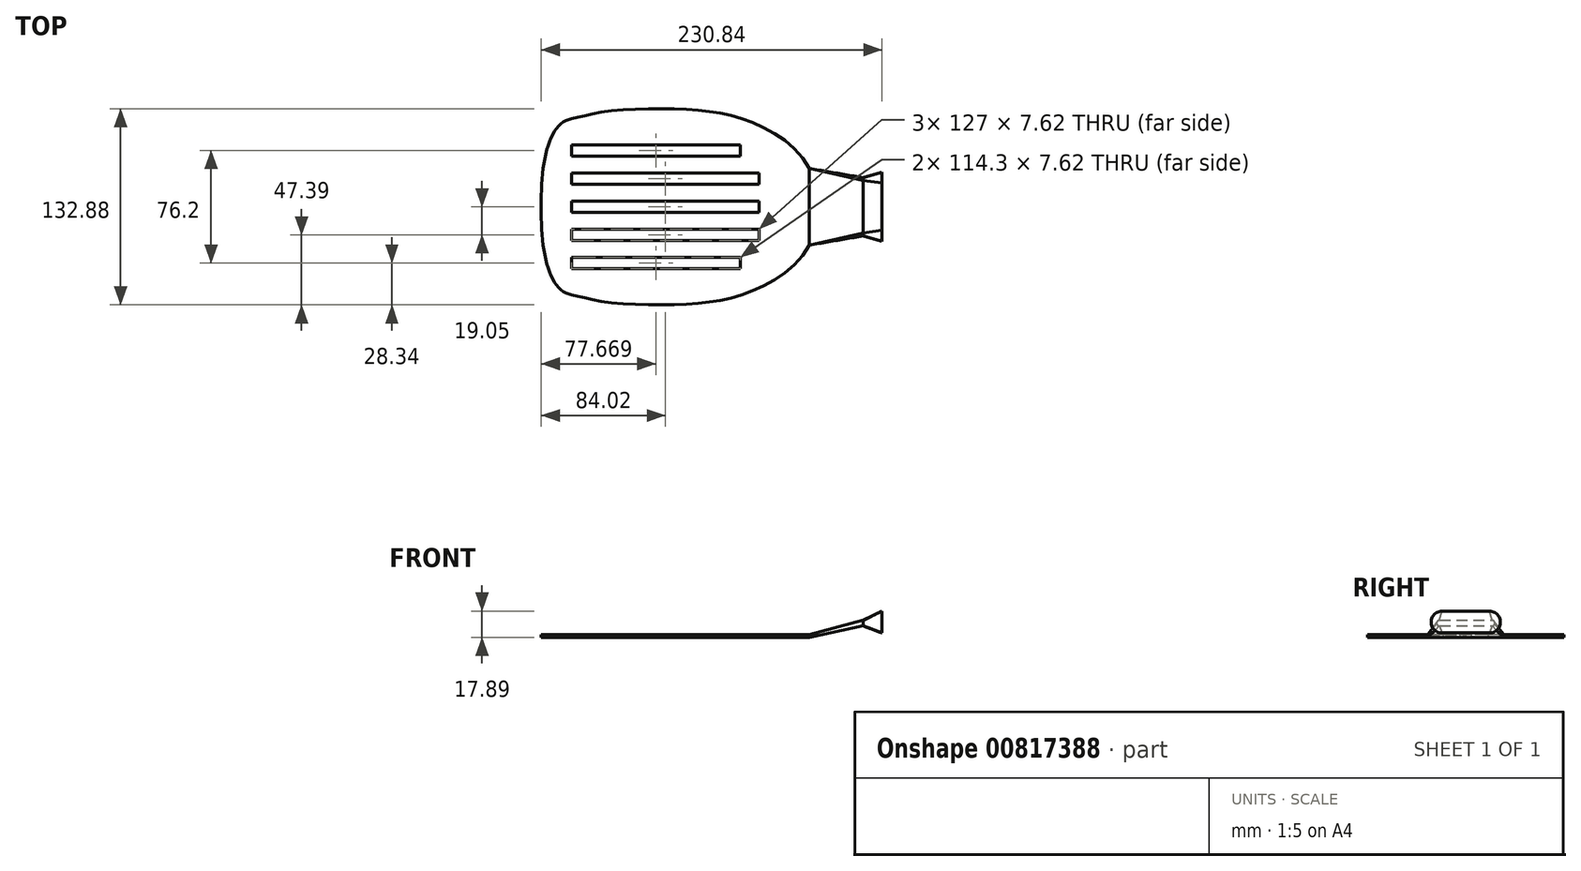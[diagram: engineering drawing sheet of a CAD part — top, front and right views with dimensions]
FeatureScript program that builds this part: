
annotation { "Feature Type Name" : "Feature", "Feature Type Description" : "" }
export const myFeature = defineFeature(function(context is Context, id is Id, definition is map)
    precondition{}
    {
        {
            var Q0;
            Q0=qCreatedBy(makeId("Top.planeOp"),FACE);
            var sketch = newSketch(context, id + "F0", { "sketchPlane" : qUnion([Q0])});
            skFitSpline(sketch, "E0", {"points": [v(-96.02, 59.7) * mm, v(-116.46, 0) * mm], "startDerivative": vector(-46.63, -8.08) * mm, "endDerivative": vector(2.49, -89.54) * mm});
            skFitSpline(sketch, "E1", {"points": [v(-96.02, 59.7) * mm, v(-75.61, 64.05) * mm, v(-21.76, 66.12) * mm, v(23.23, 58.26) * mm, v(64.98, 25.98) * mm, v(66.45, 0) * mm], "startDerivative": vector(113.32, 16.54) * mm, "endDerivative": vector(-114.65, 0) * mm});
            skFitSpline(sketch, "E2.MirrorCS", {"points": [v(-96.02, -59.7) * mm, v(-75.61, -64.05) * mm, v(-21.76, -66.12) * mm, v(23.23, -58.26) * mm, v(64.98, -25.98) * mm, v(66.45, 0) * mm], "startDerivative": vector(113.32, -16.54) * mm, "endDerivative": vector(-114.65, 0) * mm});
            skFitSpline(sketch, "E3.MirrorCS", {"points": [v(-96.02, -59.7) * mm, v(-116.46, 0) * mm], "startDerivative": vector(-46.63, 8.08) * mm, "endDerivative": vector(2.49, 89.54) * mm});
            skLineSegment(sketch, "E4", {"start": v(64.98, 25.98) * mm, "end": v(64.98, -25.98) * mm});
            skLineSegment(sketch, "E5.bottom", {"start": v(-96.02, 41.91) * mm, "end": v(18.28, 41.91) * mm});
            skLineSegment(sketch, "E5.top", {"start": v(-96.02, 34.3) * mm, "end": v(18.28, 34.3) * mm});
            skLineSegment(sketch, "E5.left", {"start": v(-96.02, 41.91) * mm, "end": v(-96.02, 34.3) * mm});
            skLineSegment(sketch, "E5.right", {"start": v(18.28, 41.91) * mm, "end": v(18.28, 34.3) * mm});
            skLineSegment(sketch, "E6.bottom", {"start": v(-96.02, 22.86) * mm, "end": v(30.98, 22.86) * mm});
            skLineSegment(sketch, "E6.top", {"start": v(-96.02, 15.24) * mm, "end": v(30.98, 15.24) * mm});
            skLineSegment(sketch, "E6.left", {"start": v(-96.02, 22.86) * mm, "end": v(-96.02, 15.24) * mm});
            skLineSegment(sketch, "E6.right", {"start": v(30.98, 22.86) * mm, "end": v(30.98, 15.24) * mm});
            skLineSegment(sketch, "E7.bottom", {"start": v(-96.02, 3.8) * mm, "end": v(30.98, 3.8) * mm});
            skLineSegment(sketch, "E7.top", {"start": v(-96.02, -3.81) * mm, "end": v(30.98, -3.81) * mm});
            skLineSegment(sketch, "E7.left", {"start": v(-96.02, 3.8) * mm, "end": v(-96.02, -3.81) * mm});
            skLineSegment(sketch, "E7.right", {"start": v(30.98, 3.8) * mm, "end": v(30.98, -3.81) * mm});
            skLineSegment(sketch, "E8.bottom", {"start": v(-96.02, -15.24) * mm, "end": v(30.98, -15.24) * mm});
            skLineSegment(sketch, "E8.top", {"start": v(-96.02, -22.86) * mm, "end": v(30.98, -22.86) * mm});
            skLineSegment(sketch, "E8.left", {"start": v(-96.02, -15.24) * mm, "end": v(-96.02, -22.86) * mm});
            skLineSegment(sketch, "E8.right", {"start": v(30.98, -15.24) * mm, "end": v(30.98, -22.86) * mm});
            skLineSegment(sketch, "E9.bottom", {"start": v(-96.02, -34.3) * mm, "end": v(18.28, -34.3) * mm});
            skLineSegment(sketch, "E9.top", {"start": v(-96.02, -41.91) * mm, "end": v(18.28, -41.91) * mm});
            skLineSegment(sketch, "E9.left", {"start": v(-96.02, -34.3) * mm, "end": v(-96.02, -41.91) * mm});
            skLineSegment(sketch, "E9.right", {"start": v(18.28, -34.3) * mm, "end": v(18.28, -41.91) * mm});
            skSolve(sketch);
        }
        {
            var Q0;
            Q0=makeQuery(id+"F0.imprint","IMPRINT",FACE,{"disambiguationData":[TD([[makeQuery(id+"F0.imprint","IMPRINT",EDGE,{"derivedFrom":sQuery(id+"F0.wireOp",EDGE,"E0")}),1.0]])]});
            extrude(context, id + "F1", {"entities" : qUnion([Q0]), "depth" : 1.9 * mm, "offsetDistance" : 25.4 * mm});
        }
        {
            var Q0;
            Q0=qCreatedBy(makeId("Right.planeOp"),FACE);
            cPlane(context, id + "F2", {"entities" : qUnion([Q0]), "cplaneType" : CPlaneType.OFFSET, "offset" : 101.6 * mm, "width" : 152.4 * mm, "height" : 152.4 * mm});
        }
        {
            var Q0;
            Q0=qCreatedBy(id+"F2.planeOp",FACE);
            var sketch = newSketch(context, id + "F3", { "sketchPlane" : qUnion([Q0])});
            skLineSegment(sketch, "E10.bottom", {"start": v(-17.82, 11.66) * mm, "end": v(17.82, 11.66) * mm});
            skLineSegment(sketch, "E10.top", {"start": v(-17.82, 7.87) * mm, "end": v(17.82, 7.87) * mm});
            skPoint(sketch, "E10.middle", {"position": v(0, 9.76) * mm});
            skArc(sketch, "E11", {"start": v(17.82, 7.87) * mm, "mid": v(19.72, 9.76) * mm, "end": v(17.82, 11.66) * mm});
            skArc(sketch, "E12", {"start": v(-17.82, 11.66) * mm, "mid": v(-19.72, 9.76) * mm, "end": v(-17.82, 7.87) * mm});
            skSolve(sketch);
        }
        {
            var Q1;
            Q1=makeQuery(id+"F1.opExtrude","SWEPT_FACE",FACE,{"disambiguationData":[OSD([sQuery(id+"F0.wireOp",EDGE,"E4")])]});
            var Q2;
            Q2=makeQuery(id+"F3.imprint","IMPRINT",FACE,{"disambiguationData":[TD([[makeQuery(id+"F3.imprint","IMPRINT",EDGE,{"derivedFrom":sQuery(id+"F3.wireOp",EDGE,"E10.bottom")}),-1.0]])]});
            loft(context, id + "F4", {"operationType" : NewBodyOperationType.ADD, "sheetProfilesArray" : [{ "sheetProfileEntities" : qUnion([Q1]) }, { "sheetProfileEntities" : qUnion([Q2]) }]});
        }
        {
            var Q0;
            Q0=qCreatedBy(id+"F2.planeOp",FACE);
            cPlane(context, id + "F5", {"entities" : qUnion([Q0]), "cplaneType" : CPlaneType.OFFSET, "offset" : 12.7 * mm, "width" : 152.4 * mm, "height" : 152.4 * mm});
        }
        {
            var Q0;
            Q0=qCreatedBy(id+"F5.planeOp",FACE);
            var sketch = newSketch(context, id + "F6", { "sketchPlane" : qUnion([Q0])});
            skLineSegment(sketch, "E13.0", {"start": v(16.03, 17.9) * mm, "end": v(-16.03, 17.9) * mm});
            skFitSpline(sketch, "E13.1", {"points": [v(16.03, 3.06) * mm, v(16.52, 3.06) * mm, v(17.24, 3.13) * mm, v(18.18, 3.37) * mm, v(18.87, 3.61) * mm, v(19.53, 3.93) * mm, v(20.16, 4.3) * mm, v(20.74, 4.73) * mm, v(21.28, 5.22) * mm, v(21.77, 5.77) * mm, v(22.2, 6.35) * mm, v(22.58, 6.97) * mm, v(22.9, 7.63) * mm, v(23.14, 8.32) * mm, v(23.31, 9.03) * mm, v(23.42, 9.74) * mm, v(23.46, 10.47) * mm, v(23.42, 11.2) * mm, v(23.31, 11.92) * mm, v(23.14, 12.63) * mm, v(22.9, 13.32) * mm, v(22.58, 13.98) * mm, v(22.2, 14.6) * mm, v(21.77, 15.18) * mm, v(21.28, 15.73) * mm, v(20.74, 16.22) * mm, v(20.15, 16.65) * mm, v(19.53, 17.02) * mm, v(18.87, 17.34) * mm, v(18.18, 17.58) * mm, v(17.24, 17.82) * mm, v(16.52, 17.9) * mm, v(16.03, 17.9) * mm]});
            skLineSegment(sketch, "E13.2", {"start": v(-16.03, 3.06) * mm, "end": v(16.03, 3.06) * mm});
            skFitSpline(sketch, "E13.3", {"points": [v(-16.03, 17.9) * mm, v(-16.52, 17.9) * mm, v(-17.24, 17.82) * mm, v(-18.18, 17.58) * mm, v(-18.87, 17.34) * mm, v(-19.53, 17.02) * mm, v(-20.16, 16.65) * mm, v(-20.74, 16.22) * mm, v(-21.28, 15.73) * mm, v(-21.77, 15.18) * mm, v(-22.2, 14.6) * mm, v(-22.58, 13.98) * mm, v(-22.9, 13.32) * mm, v(-23.14, 12.63) * mm, v(-23.31, 11.92) * mm, v(-23.42, 11.2) * mm, v(-23.46, 10.47) * mm, v(-23.42, 9.74) * mm, v(-23.31, 9.03) * mm, v(-23.14, 8.32) * mm, v(-22.9, 7.63) * mm, v(-22.58, 6.97) * mm, v(-22.2, 6.35) * mm, v(-21.77, 5.77) * mm, v(-21.28, 5.22) * mm, v(-20.74, 4.73) * mm, v(-20.15, 4.3) * mm, v(-19.53, 3.93) * mm, v(-18.87, 3.61) * mm, v(-18.18, 3.37) * mm, v(-17.24, 3.13) * mm, v(-16.52, 3.06) * mm, v(-16.03, 3.06) * mm]});
            skLineSegment(sketch, "E14", {"start": v(-4.47, 30.6) * mm, "end": v(4.47, 30.6) * mm});
            skLineSegment(sketch, "E15", {"start": v(-12.54, 25.43) * mm, "end": v(-16.03, 17.9) * mm});
            skLineSegment(sketch, "E16", {"start": v(12.54, 25.43) * mm, "end": v(16.03, 17.9) * mm});
            skPoint(sketch, "E17.visualSharp", {"position": v(-10.16, 30.6) * mm});
            skArc(sketch, "E17.filletArc", {"start": v(-4.47, 30.6) * mm, "mid": v(-9.26, 29.2) * mm, "end": v(-12.54, 25.43) * mm});
            skPoint(sketch, "E18.visualSharp", {"position": v(10.16, 30.6) * mm});
            skArc(sketch, "E18.filletArc", {"start": v(12.54, 25.43) * mm, "mid": v(9.26, 29.2) * mm, "end": v(4.47, 30.6) * mm});
            skSolve(sketch);
        }
        {
            var Q1;
            Q1=makeQuery(id+"F4.opLoft","CAP_FACE",FACE,{"disambiguationData":[OSD([makeQuery(id+"F3.imprint","IMPRINT",FACE,{"disambiguationData":[TD([[makeQuery(id+"F3.imprint","IMPRINT",EDGE,{"derivedFrom":sQuery(id+"F3.wireOp",EDGE,"E10.bottom")}),-1.0]])]})])],"isStart":true});
            var Q2;
            Q2=makeQuery(id+"F6.imprint","IMPRINT",FACE,{"disambiguationData":[TD([[makeQuery(id+"F6.imprint","IMPRINT",EDGE,{"derivedFrom":sQuery(id+"F6.wireOp",EDGE,"E13.0")}),1.0]])]});
            loft(context, id + "F7", {"operationType" : NewBodyOperationType.ADD, "sheetProfilesArray" : [{ "sheetProfileEntities" : qUnion([Q1]) }, { "sheetProfileEntities" : qUnion([Q2]) }]});
        }
        {
            var Q0;
            Q0=qCreatedBy(id+"F5.planeOp",FACE);
            cPlane(context, id + "F8", {"entities" : qUnion([Q0]), "cplaneType" : CPlaneType.OFFSET, "offset" : 203.2 * mm, "width" : 152.4 * mm, "height" : 152.4 * mm});
        }
        {
            var Q0;
            Q0=qCreatedBy(id+"F8.planeOp",FACE);
            var sketch = newSketch(context, id + "F9", { "sketchPlane" : qUnion([Q0])});
            skLineSegment(sketch, "E19", {"start": v(0, 41.43) * mm, "end": v(0, -50.53) * mm});
            skSolve(sketch);
        }
        {
            var Q0;
            Q0=qCreatedBy(id+"F8.planeOp",FACE);
            var Q1;
            Q1=sQuery(id+"F9.wireOp",EDGE,"E19");
            cPlane(context, id + "F10", {"entities" : qUnion([Q0, Q1]), "cplaneType" : CPlaneType.LINE_ANGLE, "offset" : 25.4 * mm, "angle" : 90 * degree, "width" : 152.4 * mm, "height" : 152.4 * mm});
        }
        {
            var Q0;
            Q0=qCreatedBy(id+"F10.planeOp",FACE);
            var sketch = newSketch(context, id + "F11", { "sketchPlane" : qUnion([Q0])});
            skLineSegment(sketch, "E20", {"start": v(-296.33, 42.66) * mm, "end": v(-305.24, 16.62) * mm});
            skSolve(sketch);
        }
        {
            var Q0;
            Q0=sQuery(id+"F11.wireOp",EDGE,"E20");
            extrude(context, id + "F12", {"bodyType" : ToolBodyType.SURFACE, "surfaceEntities" : qUnion([Q0]), "depth" : 25.4 * mm, "offsetDistance" : 25.4 * mm});
        }
        {
            var Q0;
            Q0=makeQuery(id+"F12.opExtrude","SWEPT_FACE",FACE,{"disambiguationData":[OSD([sQuery(id+"F11.wireOp",EDGE,"E20")])]});
            var sketch = newSketch(context, id + "F13", { "sketchPlane" : qUnion([Q0])});
            skSolve(sketch);
        }
        {
            var Q0;
            Q0=makeQuery(id+"F13.imprint","IMPRINT",FACE,{"disambiguationData":[TD([[makeQuery(id+"F13.imprint","IMPRINT",EDGE,{"derivedFrom":makeQuery(id+"F12.opExtrude","SWEPT_EDGE",EDGE,{"disambiguationData":[OSD([sQuery(id+"F11.wireOp",VERTEX,"E20.start")])]})}),-1.0]])]});
            var sketch = newSketch(context, id + "F14", { "sketchPlane" : qUnion([Q0])});
            skSolve(sketch);
        }
        {
            var Q0;
            Q0=makeQuery(id+"F14.imprint","IMPRINT",FACE,{"disambiguationData":[TD([[makeQuery(id+"F14.imprint","IMPRINT",EDGE,{"derivedFrom":makeQuery(id+"F13.imprint","IMPRINT",EDGE,{"derivedFrom":makeQuery(id+"F12.opExtrude","SWEPT_EDGE",EDGE,{"disambiguationData":[OSD([sQuery(id+"F11.wireOp",VERTEX,"E20.start")])]})})}),-1.0]])]});
            cPlane(context, id + "F15", {"entities" : qUnion([Q0]), "cplaneType" : CPlaneType.OFFSET, "offset" : 0 * mm, "width" : 152.4 * mm, "height" : 152.4 * mm});
        }
    });
